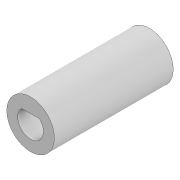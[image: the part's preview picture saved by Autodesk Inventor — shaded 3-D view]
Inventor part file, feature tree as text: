
AUTODESK INVENTOR PART (.ipt)
format: ipt  version: 2022 (Build 260153000, 153)  size: 88,064 bytes
history: native  units: mm
features: other x1, extrude x1, sketch x1
ambient origin geometry x8: Origin, YZ Plane, XZ Plane, XY Plane, X Axis, Y Axis, Z Axis, Center Point
bodies: Body1 (feature_tree)
feature tree (3):
  other  "Sólido1"
  extrude  "Extrusión1"  Depth=15.0mm
  sketch  "Boceto1"  dims[d0=6.0mm d1=3.25mm d2=2.8mm d3=15.0mm d4=0.0mm]
